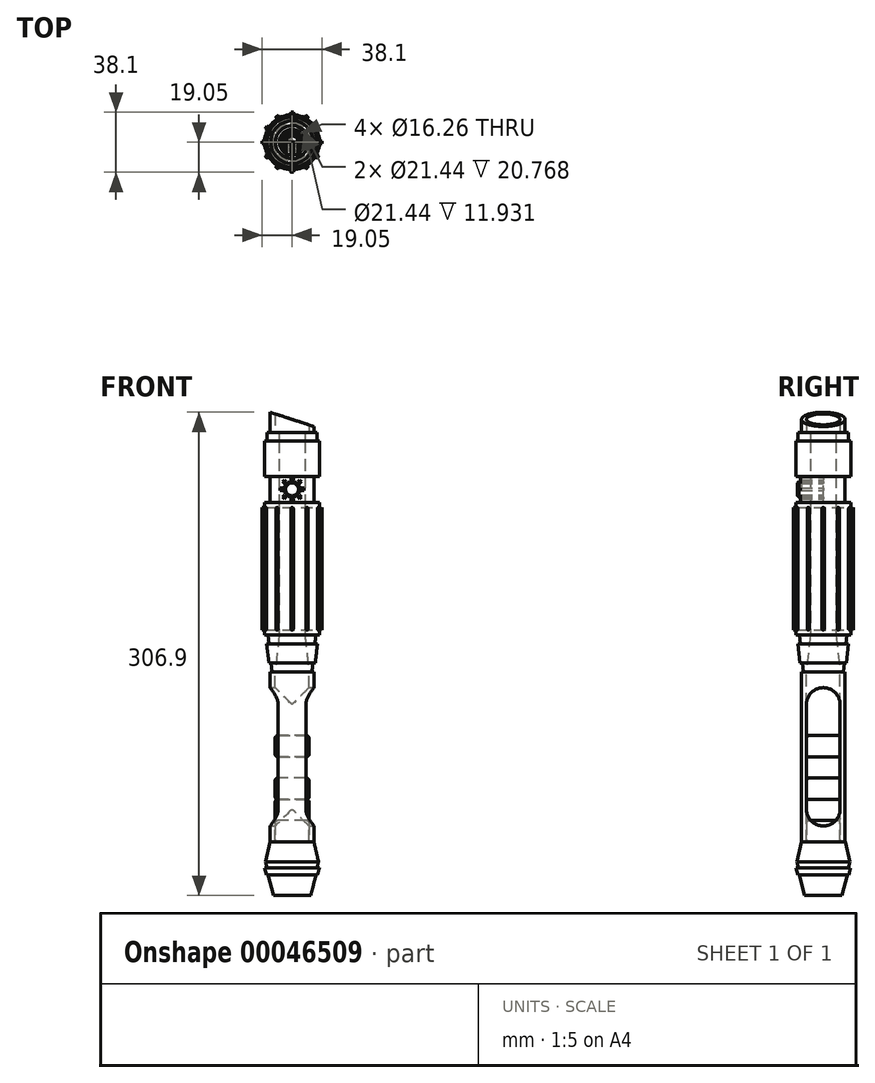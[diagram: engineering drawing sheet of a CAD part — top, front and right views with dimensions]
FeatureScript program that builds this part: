
annotation { "Feature Type Name" : "Feature", "Feature Type Description" : "" }
export const myFeature = defineFeature(function(context is Context, id is Id, definition is map)
    precondition{}
    {
        {
            var Q0;
            Q0=qCreatedBy(makeId("Top.planeOp"),FACE);
            var sketch = newSketch(context, id + "F0", { "sketchPlane" : qUnion([Q0])});
            skCircle(sketch, "E0", {"center": v(0, 0) * mm, "radius": 11.9 * mm});
            skSolve(sketch);
        }
        {
            var Q0;
            Q0=qSketchRegion(id+"F0",true);
            extrude(context, id + "F1", {"entities" : qUnion([Q0]), "depth" : 13.1 * mm, "hasDraft" : true, "draftAngle" : 14.26 * degree});
        }
        {
            var Q0;
            Q0=makeQuery(id+"F1.opExtrude","CAP_FACE",FACE,{"disambiguationData":[OSD([sQuery(id+"F0.wireOp",EDGE,"E0")])],"isStart":false});
            var sketch = newSketch(context, id + "F2", { "sketchPlane" : qUnion([Q0])});
            skCircle(sketch, "E1", {"center": v(0, 0) * mm, "radius": 16.23 * mm});
            skSolve(sketch);
        }
        {
            var Q0;
            Q0=makeQuery(id+"F2.imprint","IMPRINT",FACE,{"disambiguationData":[TD([[makeQuery(id+"F2.imprint","IMPRINT",EDGE,{"derivedFrom":sQuery(id+"F2.wireOp",EDGE,"E1")}),1.0]])]});
            var Q1;
            Q1=makeQuery(id+"F2.imprint","IMPRINT",FACE,{"disambiguationData":[TD([[makeQuery(id+"F2.imprint","IMPRINT",EDGE,{"derivedFrom":makeQuery(id+"F1.opExtrude","CAP_EDGE",EDGE,{"disambiguationData":[OSD([sQuery(id+"F0.wireOp",EDGE,"E0")])],"isStart":false})}),1.0]])]});
            var Q2;
            Q2=sQuery(id+"F2.wireOp",EDGE,"E1");
            extrude(context, id + "F3", {"entities" : qUnion([Q0, Q1]), "operationType" : NewBodyOperationType.ADD, "surfaceEntities" : qUnion([Q2]), "depth" : 4.36 * mm, "hasDraft" : true, "draftAngle" : 14.26 * degree});
        }
        {
            var Q0;
            Q0=makeQuery(id+"F3.opExtrude","CAP_FACE",FACE,{"disambiguationData":[OSD([sQuery(id+"F2.wireOp",EDGE,"E1")])],"isStart":false});
            var sketch = newSketch(context, id + "F4", { "sketchPlane" : qUnion([Q0])});
            skCircle(sketch, "E2", {"center": v(0, 0) * mm, "radius": 15.8 * mm});
            skSolve(sketch);
        }
        {
            var Q0;
            Q0=makeQuery(id+"F4.imprint","IMPRINT",FACE,{"disambiguationData":[TD([[makeQuery(id+"F4.imprint","IMPRINT",EDGE,{"derivedFrom":sQuery(id+"F4.wireOp",EDGE,"E2")}),1.0]])]});
            extrude(context, id + "F5", {"entities" : qUnion([Q0]), "operationType" : NewBodyOperationType.ADD, "depth" : 3.9 * mm, "hasDraft" : true, "draftAngle" : 14.26 * degree});
        }
        {
            var Q0;
            Q0=makeQuery(id+"F5.opExtrude","CAP_FACE",FACE,{"disambiguationData":[OSD([sQuery(id+"F4.wireOp",EDGE,"E2")])],"isStart":false});
            extrude(context, id + "F6", {"entities" : qUnion([Q0]), "operationType" : NewBodyOperationType.ADD, "depth" : 12.64 * mm});
        }
        {
            var Q0;
            Q0=makeQuery(id+"F6.opExtrude","CAP_FACE",FACE,{"disambiguationData":[OSD([sQuery(id+"F4.wireOp",EDGE,"E2")])],"isStart":false});
            chamfer(context, id + "F7", {"entities" : qUnion([Q0]), "chamferType" : ChamferType.TWO_OFFSETS, "width1" : 2.9 * mm, "oppositeDirection" : false, "width2" : 12.64 * mm, "tangentPropagation" : true});
        }
        {
            var Q0;
            Q0=makeQuery(id+"F6.opExtrude","CAP_FACE",FACE,{"disambiguationData":[OSD([sQuery(id+"F4.wireOp",EDGE,"E2")])],"isStart":false});
            var sketch = newSketch(context, id + "F8", { "sketchPlane" : qUnion([Q0])});
            skCircle(sketch, "E3", {"center": v(0, 0) * mm, "radius": 13.9 * mm});
            skSolve(sketch);
        }
        {
            var Q0;
            Q0=makeQuery(id+"F8.imprint","IMPRINT",FACE,{"disambiguationData":[TD([[makeQuery(id+"F8.imprint","IMPRINT",EDGE,{"derivedFrom":sQuery(id+"F8.wireOp",EDGE,"E3")}),1.0]])]});
            extrude(context, id + "F9", {"entities" : qUnion([Q0]), "depth" : 107.99 * mm});
        }
        {
            var Q0;
            Q0=makeQuery(id+"F9.opExtrude","CAP_FACE",FACE,{"disambiguationData":[OSD([sQuery(id+"F8.wireOp",EDGE,"E3")])],"isStart":false});
            var sketch = newSketch(context, id + "F10", { "sketchPlane" : qUnion([Q0])});
            skCircle(sketch, "E4", {"center": v(0, 0) * mm, "radius": 10.72 * mm});
            skSolve(sketch);
        }
        {
            var Q0;
            Q0=makeQuery(id+"F10.imprint","IMPRINT",FACE,{"disambiguationData":[TD([[makeQuery(id+"F10.imprint","IMPRINT",EDGE,{"derivedFrom":sQuery(id+"F10.wireOp",EDGE,"E4")}),1.0]])]});
            extrude(context, id + "F11", {"entities" : qUnion([Q0]), "operationType" : NewBodyOperationType.REMOVE, "oppositeDirection" : true, "depth" : 107.99 * mm});
        }
        {
            var Q0;
            Q0=qCreatedBy(makeId("Right.planeOp"),FACE);
            var sketch = newSketch(context, id + "F12", { "sketchPlane" : qUnion([Q0])});
            skCircle(sketch, "E5", {"center": v(0, 121.23) * mm, "radius": 10.72 * mm});
            skCircle(sketch, "E6", {"center": v(0, 54.78) * mm, "radius": 10.72 * mm});
            skLineSegment(sketch, "E7", {"start": v(0, 121.23) * mm, "end": v(10.72, 121.23) * mm});
            skLineSegment(sketch, "E8", {"start": v(0, 54.78) * mm, "end": v(-10.72, 54.78) * mm});
            skLineSegment(sketch, "E9.bottom", {"start": v(-10.72, 54.78) * mm, "end": v(10.72, 54.78) * mm});
            skLineSegment(sketch, "E9.top", {"start": v(-10.72, 121.23) * mm, "end": v(10.72, 121.23) * mm});
            skLineSegment(sketch, "E9.left", {"start": v(-10.72, 54.78) * mm, "end": v(-10.72, 121.23) * mm});
            skLineSegment(sketch, "E9.right", {"start": v(10.72, 54.78) * mm, "end": v(10.72, 121.23) * mm});
            skSolve(sketch);
        }
        {
            var Q0;
            Q0=qSketchRegion(id+"F12",true);
            extrude(context, id + "F13", {"entities" : qUnion([Q0]), "operationType" : NewBodyOperationType.REMOVE, "endBound" : BoundingType.SYMMETRIC, "oppositeDirection" : true, "depth" : 27.79 * mm});
        }
        {
            var Q0;
            Q0=makeQuery(id+"F6.opExtrude","CAP_FACE",FACE,{"disambiguationData":[OSD([sQuery(id+"F4.wireOp",EDGE,"E2")])],"isStart":false});
            var sketch = newSketch(context, id + "F14", { "sketchPlane" : qUnion([Q0])});
            skCircle(sketch, "E10", {"center": v(0, 0) * mm, "radius": 10.72 * mm});
            skSolve(sketch);
        }
        {
            var Q0;
            Q0=makeQuery(id+"F14.imprint","IMPRINT",FACE,{"disambiguationData":[TD([[makeQuery(id+"F14.imprint","IMPRINT",EDGE,{"derivedFrom":sQuery(id+"F14.wireOp",EDGE,"E10")}),1.0]])]});
            var Q1;
            Q1=sQuery(id+"F14.wireOp",EDGE,"E10");
            extrude(context, id + "F15", {"entities" : qUnion([Q0]), "surfaceEntities" : qUnion([Q1]), "depth" : 13.5 * mm});
        }
        {
            var Q0;
            Q0=makeQuery(id+"F15.opExtrude","CAP_FACE",FACE,{"disambiguationData":[OSD([sQuery(id+"F14.wireOp",EDGE,"E10")])],"isStart":false});
            fillet(context, id + "F16", {"entities" : qUnion([Q0]), "radius" : 1.59 * mm, "tangentPropagation" : true, "allowEdgeOverflow" : false});
        }
        {
            var Q0;
            Q0=makeQuery(id+"F15.opExtrude","CAP_EDGE",EDGE,{"disambiguationData":[OSD([sQuery(id+"F14.wireOp",EDGE,"E10")])],"isStart":true});
            fillet(context, id + "F17", {"entities" : qUnion([Q0]), "radius" : 1.59 * mm, "tangentPropagation" : true, "allowEdgeOverflow" : false});
        }
        {
            var Q0;
            Q0=makeQuery(id+"F15.opExtrude","SWEPT_BODY",BODY,{"disambiguationData":[OSD([sQuery(id+"F14.wireOp",EDGE,"E10")])]});
            transform(context, id + "F18", {"entities" : qUnion([Q0]), "transformType" : TransformType.TRANSLATION_3D, "dx" : 0 * mm, "dy" : 0 * mm, "dz" : 13.5 * mm, "makeCopy" : true});
        }
        {
            var Q0;
            Q0=makeQuery(id+"F15.opExtrude","SWEPT_BODY",BODY,{"disambiguationData":[OSD([sQuery(id+"F14.wireOp",EDGE,"E10")])]});
            transform(context, id + "F19", {"entities" : qUnion([Q0]), "transformType" : TransformType.TRANSLATION_3D, "dx" : 0 * mm, "dy" : 0 * mm, "dz" : 27 * mm, "makeCopy" : true});
        }
        {
            var Q0;
            Q0=makeQuery(id+"F15.opExtrude","SWEPT_BODY",BODY,{"disambiguationData":[OSD([sQuery(id+"F14.wireOp",EDGE,"E10")])]});
            transform(context, id + "F20", {"entities" : qUnion([Q0]), "transformType" : TransformType.TRANSLATION_3D, "dx" : 0 * mm, "dy" : 0 * mm, "dz" : 54 * mm, "makeCopy" : true});
        }
        {
            var Q0;
            Q0=makeQuery(id+"F9.opExtrude","CAP_FACE",FACE,{"disambiguationData":[OSD([sQuery(id+"F8.wireOp",EDGE,"E3")])],"isStart":false});
            var sketch = newSketch(context, id + "F21", { "sketchPlane" : qUnion([Q0])});
            skCircle(sketch, "E11", {"center": v(0, 0) * mm, "radius": 12.64 * mm});
            skSolve(sketch);
        }
        {
            var Q0;
            Q0=makeQuery(id+"F21.imprint","IMPRINT",FACE,{"disambiguationData":[TD([[makeQuery(id+"F21.imprint","IMPRINT",EDGE,{"derivedFrom":sQuery(id+"F21.wireOp",EDGE,"E11")}),1.0]])]});
            var Q1;
            Q1=makeQuery(id+"F21.imprint","IMPRINT",FACE,{"disambiguationData":[TD([[makeQuery(id+"F21.imprint","IMPRINT",EDGE,{"derivedFrom":makeQuery(id+"F11.boolean.opBoolean","COPY",EDGE,{"derivedFrom":makeQuery(id+"F11.opExtrude","CAP_EDGE",EDGE,{"disambiguationData":[OSD([sQuery(id+"F10.wireOp",EDGE,"E4")])],"isStart":true})})}),1.0]])]});
            extrude(context, id + "F22", {"entities" : qUnion([Q0, Q1]), "depth" : 5.7 * mm, "hasDraft" : true, "draftAngle" : 6.33 * degree});
        }
        {
            var Q0;
            Q0=makeQuery(id+"F22.opExtrude","CAP_FACE",FACE,{"disambiguationData":[OSD([sQuery(id+"F21.wireOp",EDGE,"E11")])],"isStart":false});
            var sketch = newSketch(context, id + "F23", { "sketchPlane" : qUnion([Q0])});
            skCircle(sketch, "E12", {"center": v(0, 0) * mm, "radius": 14.76 * mm});
            skSolve(sketch);
        }
        {
            var Q0;
            Q0=makeQuery(id+"F23.imprint","IMPRINT",FACE,{"disambiguationData":[TD([[makeQuery(id+"F23.imprint","IMPRINT",EDGE,{"derivedFrom":makeQuery(id+"F22.opExtrude","CAP_EDGE",EDGE,{"disambiguationData":[OSD([sQuery(id+"F21.wireOp",EDGE,"E11")])],"isStart":false})}),1.0]])]});
            var Q1;
            Q1=makeQuery(id+"F23.imprint","IMPRINT",FACE,{"disambiguationData":[TD([[makeQuery(id+"F23.imprint","IMPRINT",EDGE,{"derivedFrom":sQuery(id+"F23.wireOp",EDGE,"E12")}),1.0]])]});
            extrude(context, id + "F24", {"entities" : qUnion([Q0, Q1]), "operationType" : NewBodyOperationType.ADD, "depth" : 11.93 * mm, "hasDraft" : true, "draftAngle" : 6.33 * degree});
        }
        {
            var Q0;
            Q0=makeQuery(id+"F24.opExtrude","CAP_FACE",FACE,{"disambiguationData":[OSD([sQuery(id+"F23.wireOp",EDGE,"E12")])],"isStart":false});
            var sketch = newSketch(context, id + "F25", { "sketchPlane" : qUnion([Q0])});
            skCircle(sketch, "E13", {"center": v(0, 0) * mm, "radius": 14.47 * mm});
            skSolve(sketch);
        }
        {
            var Q0;
            Q0=makeQuery(id+"F25.imprint","IMPRINT",FACE,{"disambiguationData":[TD([[makeQuery(id+"F25.imprint","IMPRINT",EDGE,{"derivedFrom":sQuery(id+"F25.wireOp",EDGE,"E13")}),1.0]])]});
            extrude(context, id + "F26", {"entities" : qUnion([Q0]), "operationType" : NewBodyOperationType.ADD, "depth" : 5.7 * mm, "hasDraft" : true, "draftAngle" : 6.33 * degree});
        }
        {
            var Q0;
            Q0=makeQuery(id+"F26.opExtrude","CAP_FACE",FACE,{"disambiguationData":[OSD([sQuery(id+"F25.wireOp",EDGE,"E13")])],"isStart":false});
            var sketch = newSketch(context, id + "F27", { "sketchPlane" : qUnion([Q0])});
            skCircle(sketch, "E14", {"center": v(0, 0) * mm, "radius": 17.44 * mm});
            skSolve(sketch);
        }
        {
            var Q0;
            Q0=makeQuery(id+"F27.imprint","IMPRINT",FACE,{"disambiguationData":[TD([[makeQuery(id+"F27.imprint","IMPRINT",EDGE,{"derivedFrom":sQuery(id+"F27.wireOp",EDGE,"E14")}),1.0]])]});
            var Q1;
            Q1=makeQuery(id+"F27.imprint","IMPRINT",FACE,{"disambiguationData":[TD([[makeQuery(id+"F27.imprint","IMPRINT",EDGE,{"derivedFrom":makeQuery(id+"F26.opExtrude","CAP_EDGE",EDGE,{"disambiguationData":[OSD([sQuery(id+"F25.wireOp",EDGE,"E13")])],"isStart":false})}),1.0]])]});
            extrude(context, id + "F28", {"entities" : qUnion([Q0, Q1]), "depth" : 84.34 * mm});
        }
        {
            var Q0;
            Q0=qCreatedBy(makeId("Front.planeOp"),FACE);
            var sketch = newSketch(context, id + "F29", { "sketchPlane" : qUnion([Q0])});
            skCircle(sketch, "E15", {"center": v(0, 245.68) * mm, "radius": 0.8 * mm});
            skCircle(sketch, "E16", {"center": v(0, 169.27) * mm, "radius": 0.8 * mm});
            skLineSegment(sketch, "E17", {"start": v(0, 245.68) * mm, "end": v(0.8, 245.68) * mm});
            skLineSegment(sketch, "E18", {"start": v(0, 169.27) * mm, "end": v(-0.8, 169.27) * mm});
            skLineSegment(sketch, "E19.bottom", {"start": v(-0.8, 169.27) * mm, "end": v(0.8, 169.27) * mm});
            skLineSegment(sketch, "E19.top", {"start": v(-0.8, 245.68) * mm, "end": v(0.8, 245.68) * mm});
            skLineSegment(sketch, "E19.left", {"start": v(-0.8, 169.27) * mm, "end": v(-0.8, 245.68) * mm});
            skLineSegment(sketch, "E19.right", {"start": v(0.8, 169.27) * mm, "end": v(0.8, 245.68) * mm});
            skSolve(sketch);
        }
        {
            var Q0;
            Q0=qSketchRegion(id+"F29",true);
            extrude(context, id + "F30", {"entities" : qUnion([Q0]), "endBound" : BoundingType.SYMMETRIC, "depth" : 38.1 * mm});
        }
        {
            var Q0;
            Q0=makeQuery(id+"F30.opExtrude","SWEPT_BODY",BODY,{"disambiguationData":[OSD([sQuery(id+"F29.wireOp",EDGE,"E15"),sQuery(id+"F29.wireOp",EDGE,"E16"),sQuery(id+"F29.wireOp",EDGE,"E19.left"),sQuery(id+"F29.wireOp",EDGE,"E19.right")])]});
            var Q1;
            Q1=makeQuery(id+"F28.opExtrude","SWEPT_FACE",FACE,{"disambiguationData":[OSD([sQuery(id+"F27.wireOp",EDGE,"E14")])]});
            circularPattern(context, id + "F31", {"entities" : qUnion([Q0]), "axis" : qUnion([Q1]), "angle" : 30 * degree, "instanceCount" : round(6)});
        }
        {
            var Q0;
            Q0=makeQuery(id+"F28.opExtrude","CAP_FACE",FACE,{"disambiguationData":[OSD([sQuery(id+"F27.wireOp",EDGE,"E14")])],"isStart":false});
            var sketch = newSketch(context, id + "F32", { "sketchPlane" : qUnion([Q0])});
            skCircle(sketch, "E20", {"center": v(0, 0) * mm, "radius": 13.9 * mm});
            skSolve(sketch);
        }
        {
            var Q0;
            Q0=makeQuery(id+"F32.imprint","IMPRINT",FACE,{"disambiguationData":[TD([[makeQuery(id+"F32.imprint","IMPRINT",EDGE,{"derivedFrom":sQuery(id+"F32.wireOp",EDGE,"E20")}),1.0]])]});
            extrude(context, id + "F33", {"entities" : qUnion([Q0]), "depth" : 16.55 * mm});
        }
        {
            var Q0;
            Q0=makeQuery(id+"F33.opExtrude","CAP_FACE",FACE,{"disambiguationData":[OSD([sQuery(id+"F32.wireOp",EDGE,"E20")])],"isStart":false});
            var sketch = newSketch(context, id + "F34", { "sketchPlane" : qUnion([Q0])});
            skCircle(sketch, "E21", {"center": v(0, 0) * mm, "radius": 17.44 * mm});
            skSolve(sketch);
        }
        {
            var Q0;
            Q0=makeQuery(id+"F34.imprint","IMPRINT",FACE,{"disambiguationData":[TD([[makeQuery(id+"F34.imprint","IMPRINT",EDGE,{"derivedFrom":sQuery(id+"F34.wireOp",EDGE,"E21")}),1.0]])]});
            var Q1;
            Q1=makeQuery(id+"F34.imprint","IMPRINT",FACE,{"disambiguationData":[TD([[makeQuery(id+"F34.imprint","IMPRINT",EDGE,{"derivedFrom":makeQuery(id+"F33.opExtrude","CAP_EDGE",EDGE,{"disambiguationData":[OSD([sQuery(id+"F32.wireOp",EDGE,"E20")])],"isStart":false})}),1.0]])]});
            extrude(context, id + "F35", {"entities" : qUnion([Q0, Q1]), "depth" : 22.46 * mm});
        }
        {
            var Q0;
            Q0=makeQuery(id+"F35.opExtrude","CAP_FACE",FACE,{"disambiguationData":[OSD([sQuery(id+"F34.wireOp",EDGE,"E21")])],"isStart":false});
            var sketch = newSketch(context, id + "F36", { "sketchPlane" : qUnion([Q0])});
            skCircle(sketch, "E22", {"center": v(0, 0) * mm, "radius": 15.96 * mm});
            skSolve(sketch);
        }
        {
            var Q0;
            Q0=makeQuery(id+"F36.imprint","IMPRINT",FACE,{"disambiguationData":[TD([[makeQuery(id+"F36.imprint","IMPRINT",EDGE,{"derivedFrom":sQuery(id+"F36.wireOp",EDGE,"E22")}),1.0]])]});
            extrude(context, id + "F37", {"entities" : qUnion([Q0]), "depth" : 5.32 * mm});
        }
        {
            var Q0;
            Q0=makeQuery(id+"F37.opExtrude","CAP_FACE",FACE,{"disambiguationData":[OSD([sQuery(id+"F36.wireOp",EDGE,"E22")])],"isStart":false});
            var sketch = newSketch(context, id + "F38", { "sketchPlane" : qUnion([Q0])});
            skCircle(sketch, "E23", {"center": v(0, 0) * mm, "radius": 13.9 * mm});
            skSolve(sketch);
        }
        {
            var Q0;
            Q0=makeQuery(id+"F38.imprint","IMPRINT",FACE,{"disambiguationData":[TD([[makeQuery(id+"F38.imprint","IMPRINT",EDGE,{"derivedFrom":sQuery(id+"F38.wireOp",EDGE,"E23")}),1.0]])]});
            extrude(context, id + "F39", {"entities" : qUnion([Q0]), "depth" : 12.92 * mm});
        }
        {
            var Q0;
            Q0=qCreatedBy(makeId("Front.planeOp"),FACE);
            var sketch = newSketch(context, id + "F40", { "sketchPlane" : qUnion([Q0])});
            skLineSegment(sketch, "E24", {"start": v(-13.9, 306.9) * mm, "end": v(13.9, 297.84) * mm});
            skLineSegment(sketch, "E25", {"start": v(13.9, 297.84) * mm, "end": v(13.9, 314.05) * mm});
            skLineSegment(sketch, "E26", {"start": v(13.9, 314.05) * mm, "end": v(-13.9, 306.9) * mm});
            skLineSegment(sketch, "E27", {"start": v(0, 307) * mm, "end": v(0, 299.85) * mm});
            skSolve(sketch);
        }
        {
            var Q0;
            Q0=qSketchRegion(id+"F40",true);
            extrude(context, id + "F41", {"entities" : qUnion([Q0]), "operationType" : NewBodyOperationType.REMOVE, "endBound" : BoundingType.SYMMETRIC, "oppositeDirection" : true, "depth" : 50.8 * mm});
        }
        {
            var Q0;
            Q0=makeQuery(id+"F37.opExtrude","CAP_FACE",FACE,{"disambiguationData":[OSD([sQuery(id+"F36.wireOp",EDGE,"E22")])],"isStart":false});
            var sketch = newSketch(context, id + "F42", { "sketchPlane" : qUnion([Q0])});
            skCircle(sketch, "E28", {"center": v(0, 0) * mm, "radius": 10.72 * mm});
            skSolve(sketch);
        }
        {
            var Q0;
            Q0=qSketchRegion(id+"F42",true);
            extrude(context, id + "F43", {"entities" : qUnion([Q0]), "operationType" : NewBodyOperationType.REMOVE, "depth" : 25.4 * mm});
        }
        {
            var Q0;
            Q0=qCreatedBy(makeId("Front.planeOp"),FACE);
            var sketch = newSketch(context, id + "F44", { "sketchPlane" : qUnion([Q0])});
            skCircle(sketch, "E29", {"center": v(0, 257.92) * mm, "radius": 5.08 * mm});
            skSolve(sketch);
        }
        {
            var Q0;
            Q0=qSketchRegion(id+"F44",true);
            extrude(context, id + "F45", {"entities" : qUnion([Q0]), "depth" : 16.5 * mm});
        }
        {
            var Q0;
            Q0=makeQuery(id+"F45.opExtrude","CAP_EDGE",EDGE,{"disambiguationData":[OSD([sQuery(id+"F44.wireOp",EDGE,"E29")])],"isStart":false});
            chamfer(context, id + "F46", {"entities" : qUnion([Q0]), "width" : 1.02 * mm, "tangentPropagation" : true});
        }
        {
            var Q0;
            Q0=qCreatedBy(makeId("Front.planeOp"),FACE);
            var sketch = newSketch(context, id + "F47", { "sketchPlane" : qUnion([Q0])});
            skLineSegment(sketch, "E30.rect.bottom", {"start": v(0.8, 265.56) * mm, "end": v(-0.8, 265.56) * mm});
            skLineSegment(sketch, "E30.rect.top", {"start": v(0.8, 263.97) * mm, "end": v(-0.8, 263.97) * mm});
            skLineSegment(sketch, "E30.rect.left", {"start": v(0.8, 265.56) * mm, "end": v(0.8, 263.97) * mm});
            skLineSegment(sketch, "E30.rect.right", {"start": v(-0.8, 265.56) * mm, "end": v(-0.8, 263.97) * mm});
            skPoint(sketch, "E30.rect.middle", {"position": v(0, 264.77) * mm});
            skSolve(sketch);
        }
        {
            var Q0;
            Q0=qSketchRegion(id+"F47",true);
            extrude(context, id + "F48", {"entities" : qUnion([Q0]), "depth" : 14.48 * mm});
        }
        {
            var Q0;
            Q0=makeQuery(id+"F48.opExtrude","SWEPT_BODY",BODY,{"disambiguationData":[OSD([sQuery(id+"F47.wireOp",EDGE,"E30.rect.bottom"),sQuery(id+"F47.wireOp",EDGE,"E30.rect.top"),sQuery(id+"F47.wireOp",EDGE,"E30.rect.left"),sQuery(id+"F47.wireOp",EDGE,"E30.rect.right")])]});
            var Q1;
            {var subQ0=sQuery(id+"F44.wireOp",EDGE,"E29");Q1=makeQuery(id+"F46.opChamfer","BLEND_EDGE",EDGE,{"blendedFrom":[makeQuery(id+"F45.opExtrude","CAP_EDGE",EDGE,{"disambiguationData":[OSD([subQ0])],"isStart":false}),makeQuery(id+"F45.opExtrude","CAP_FACE",FACE,{"disambiguationData":[OSD([subQ0])],"isStart":false})],"blendedInto":[makeQuery(id+"F45.opExtrude","CAP_FACE",FACE,{"disambiguationData":[OSD([subQ0])],"isStart":false})]});}
            circularPattern(context, id + "F49", {"entities" : qUnion([Q0]), "axis" : qUnion([Q1]), "angle" : 45 * degree, "instanceCount" : round(8)});
        }
    });
